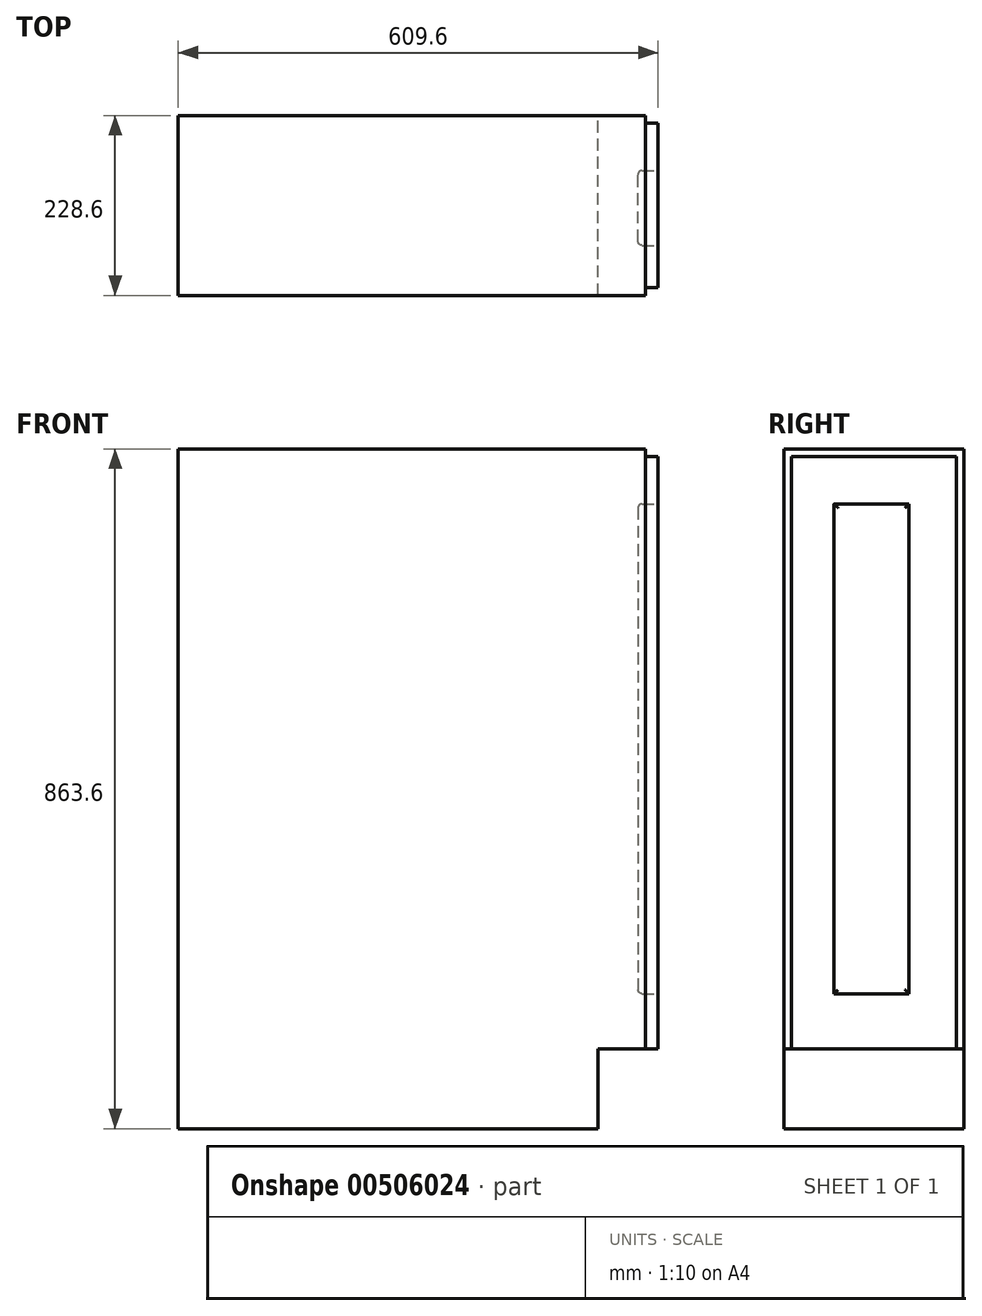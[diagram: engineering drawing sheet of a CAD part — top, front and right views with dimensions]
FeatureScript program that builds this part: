
annotation { "Feature Type Name" : "Feature", "Feature Type Description" : "" }
export const myFeature = defineFeature(function(context is Context, id is Id, definition is map)
    precondition{}
    {
        {
            var Q0;
            Q0=qCreatedBy(makeId("Top.planeOp"),FACE);
            var sketch = newSketch(context, id + "F0", { "sketchPlane" : qUnion([Q0])});
            skLineSegment(sketch, "E0.bottom", {"start": v(0, 0) * mm, "end": v(-609.6, 0) * mm});
            skLineSegment(sketch, "E0.top", {"start": v(0, 228.6) * mm, "end": v(-609.6, 228.6) * mm});
            skLineSegment(sketch, "E0.left", {"start": v(0, 0) * mm, "end": v(0, 228.6) * mm});
            skLineSegment(sketch, "E0.right", {"start": v(-609.6, 0) * mm, "end": v(-609.6, 228.6) * mm});
            skSolve(sketch);
        }
        {
            var Q0;
            Q0=makeQuery(id+"F0.imprint","IMPRINT",FACE,{"disambiguationData":[TD([[makeQuery(id+"F0.imprint","IMPRINT",EDGE,{"derivedFrom":sQuery(id+"F0.wireOp",EDGE,"E0.bottom")}),-1.0]])]});
            extrude(context, id + "F1", {"entities" : qUnion([Q0]), "depth" : 863.6 * mm, "offsetDistance" : 25.4 * mm});
        }
        {
            var Q0;
            Q0=makeQuery(id+"F1.opExtrude","SWEPT_FACE",FACE,{"disambiguationData":[OSD([sQuery(id+"F0.wireOp",EDGE,"E0.left")])]});
            var sketch = newSketch(context, id + "F2", { "sketchPlane" : qUnion([Q0])});
            skLineSegment(sketch, "E1.bottom", {"start": v(63.5, 793.75) * mm, "end": v(158.75, 793.75) * mm});
            skLineSegment(sketch, "E1.top", {"start": v(63.5, 171.45) * mm, "end": v(158.75, 171.45) * mm});
            skLineSegment(sketch, "E1.left", {"start": v(63.5, 793.75) * mm, "end": v(63.5, 171.45) * mm});
            skLineSegment(sketch, "E1.right", {"start": v(158.75, 793.75) * mm, "end": v(158.75, 171.45) * mm});
            skSolve(sketch);
        }
        {
            var Q0;
            Q0 = qSketchRegion(id + "F2", true);
            extrude(context, id + "F3", {"entities" : qUnion([Q0]), "operationType" : NewBodyOperationType.REMOVE, "oppositeDirection" : true, "depth" : 25.4 * mm, "offsetDistance" : 25.4 * mm});
        }
        {
            var Q0;
            Q0=makeQuery(id+"F3.boolean.opBoolean","COPY",FACE,{"derivedFrom":makeQuery(id+"F3.opExtrude","CAP_FACE",FACE,{"disambiguationData":[OSD([sQuery(id+"F2.wireOp",EDGE,"E1.bottom"),sQuery(id+"F2.wireOp",EDGE,"E1.top"),sQuery(id+"F2.wireOp",EDGE,"E1.left"),sQuery(id+"F2.wireOp",EDGE,"E1.right")])],"isStart":false})});
            fillet(context, id + "F4", {"entities" : qUnion([Q0]), "radius" : 5.08 * mm, "tangentPropagation" : true, "allowEdgeOverflow" : false});
        }
        {
            var Q0;
            Q0=makeQuery(id+"F1.opExtrude","SWEPT_FACE",FACE,{"disambiguationData":[OSD([sQuery(id+"F0.wireOp",EDGE,"E0.left")])]});
            var sketch = newSketch(context, id + "F5", { "sketchPlane" : qUnion([Q0])});
            skLineSegment(sketch, "E2.bottom", {"start": v(0, 101.6) * mm, "end": v(228.6, 101.6) * mm});
            skLineSegment(sketch, "E2.top", {"start": v(0, 0) * mm, "end": v(228.6, 0) * mm});
            skLineSegment(sketch, "E2.left", {"start": v(0, 101.6) * mm, "end": v(0, 0) * mm});
            skLineSegment(sketch, "E2.right", {"start": v(228.6, 101.6) * mm, "end": v(228.6, 0) * mm});
            skSolve(sketch);
        }
        {
            var Q0;
            Q0 = qSketchRegion(id + "F5", true);
            extrude(context, id + "F6", {"entities" : qUnion([Q0]), "operationType" : NewBodyOperationType.REMOVE, "oppositeDirection" : true, "depth" : 76.2 * mm, "offsetDistance" : 25.4 * mm});
        }
        {
            var Q0;
            Q0=makeQuery(id+"F1.opExtrude","SWEPT_FACE",FACE,{"disambiguationData":[OSD([sQuery(id+"F0.wireOp",EDGE,"E0.left")])]});
            var sketch = newSketch(context, id + "F7", { "sketchPlane" : qUnion([Q0])});
            skLineSegment(sketch, "E3.bottom", {"start": v(9.65, 853.95) * mm, "end": v(218.95, 853.95) * mm});
            skLineSegment(sketch, "E3.top", {"start": v(9.65, 94.4) * mm, "end": v(218.95, 94.4) * mm});
            skLineSegment(sketch, "E3.left", {"start": v(9.65, 853.95) * mm, "end": v(9.65, 94.4) * mm});
            skLineSegment(sketch, "E3.right", {"start": v(218.95, 853.95) * mm, "end": v(218.95, 94.4) * mm});
            skLineSegment(sketch, "E4.bottom", {"start": v(0, 863.6) * mm, "end": v(228.6, 863.6) * mm});
            skLineSegment(sketch, "E4.top", {"start": v(0, 84.74) * mm, "end": v(228.6, 84.74) * mm});
            skLineSegment(sketch, "E4.left", {"start": v(0, 863.6) * mm, "end": v(0, 84.74) * mm});
            skLineSegment(sketch, "E4.right", {"start": v(228.6, 863.6) * mm, "end": v(228.6, 84.74) * mm});
            skSolve(sketch);
        }
        {
            var Q0;
            Q0=makeQuery(id+"F7.imprint","IMPRINT",FACE,{"disambiguationData":[TD([[makeQuery(id+"F7.imprint","IMPRINT",EDGE,{"derivedFrom":sQuery(id+"F7.wireOp",EDGE,"E3.bottom")}),1.0]])]});
            extrude(context, id + "F8", {"entities" : qUnion([Q0]), "operationType" : NewBodyOperationType.REMOVE, "oppositeDirection" : true, "depth" : 15.88 * mm, "offsetDistance" : 25.4 * mm});
        }
    });
